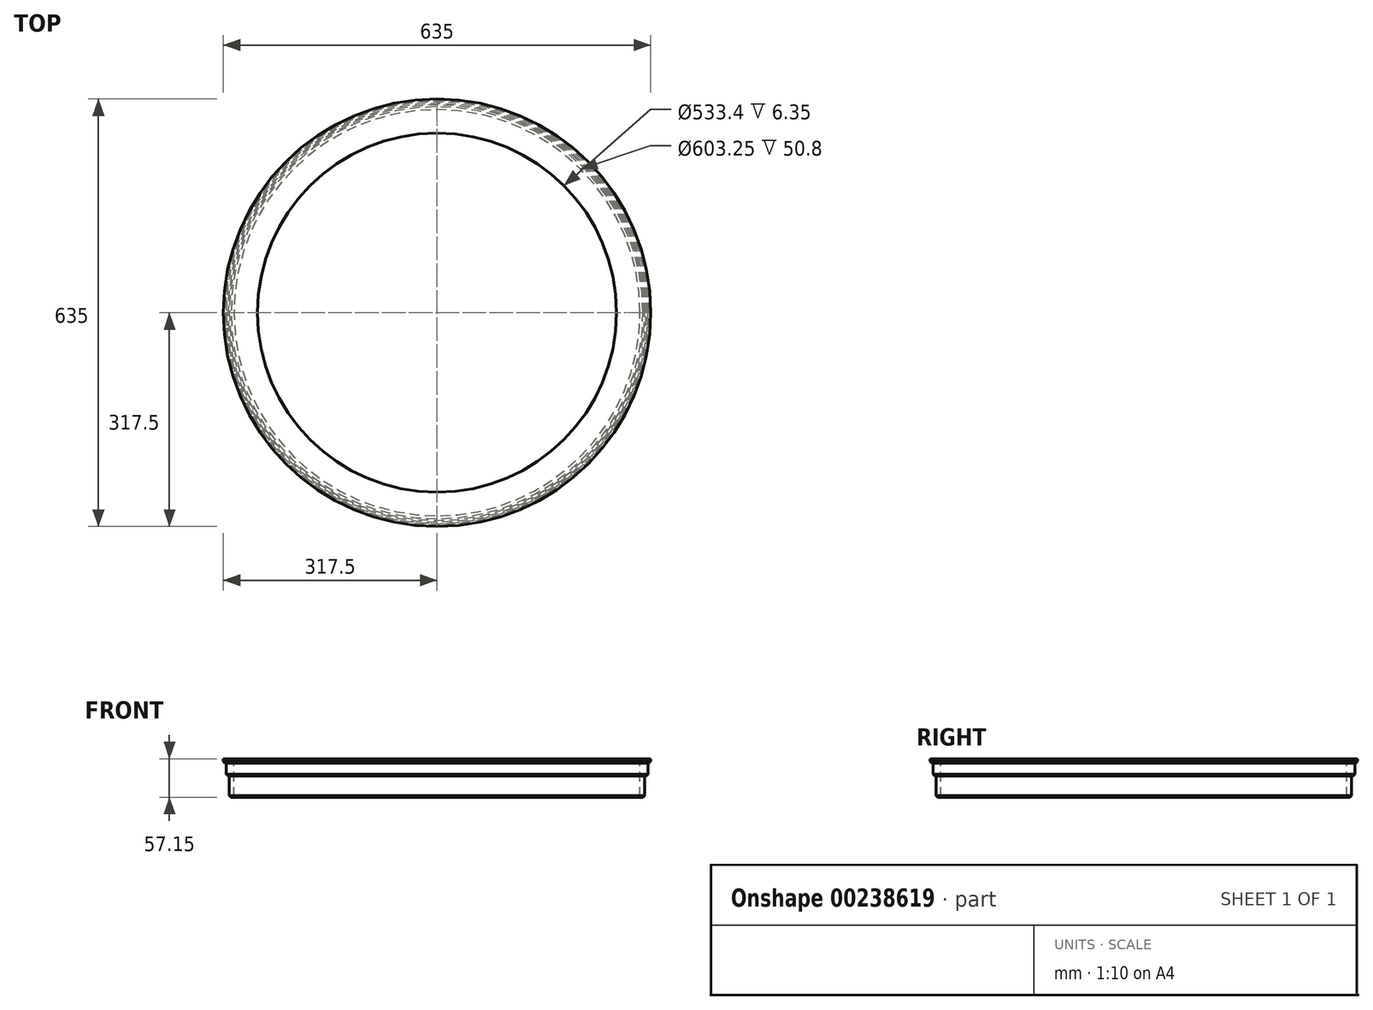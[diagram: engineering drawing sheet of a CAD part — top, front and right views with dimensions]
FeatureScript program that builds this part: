
annotation { "Feature Type Name" : "Feature", "Feature Type Description" : "" }
export const myFeature = defineFeature(function(context is Context, id is Id, definition is map)
    precondition{}
    {
        {
            var Q0;
            Q0=qCreatedBy(makeId("Top.planeOp"),FACE);
            var sketch = newSketch(context, id + "F0", { "sketchPlane" : qUnion([Q0])});
            skCircle(sketch, "E0", {"center": v(0, 0) * mm, "radius": 317.5 * mm});
            skCircle(sketch, "E1", {"center": v(0, 0) * mm, "radius": 266.7 * mm});
            skSolve(sketch);
        }
        {
            var Q0;
            Q0=makeQuery(id+"F0.imprint","IMPRINT",FACE,{"disambiguationData":[TD([[makeQuery(id+"F0.imprint","IMPRINT",EDGE,{"derivedFrom":sQuery(id+"F0.wireOp",EDGE,"E0")}),1.0]])]});
            extrude(context, id + "F1", {"entities" : qUnion([Q0]), "depth" : 6.35 * mm});
        }
        {
            var Q0;
            Q0=makeQuery(id+"F1.opExtrude","CAP_FACE",FACE,{"disambiguationData":[OSD([sQuery(id+"F0.wireOp",EDGE,"E0"),sQuery(id+"F0.wireOp",EDGE,"E1")])],"isStart":true});
            var sketch = newSketch(context, id + "F2", { "sketchPlane" : qUnion([Q0])});
            skCircle(sketch, "E2", {"center": v(0, 0) * mm, "radius": 301.63 * mm});
            skCircle(sketch, "E3", {"center": v(0, 0) * mm, "radius": 308.61 * mm});
            skCircle(sketch, "E4", {"center": v(0, 0) * mm, "radius": 313.38 * mm});
            skSolve(sketch);
        }
        {
            var Q0;
            Q0=makeQuery(id+"F2.imprint","IMPRINT",FACE,{"disambiguationData":[TD([[makeQuery(id+"F2.imprint","IMPRINT",EDGE,{"derivedFrom":sQuery(id+"F2.wireOp",EDGE,"E2")}),-1.0]])]});
            extrude(context, id + "F3", {"entities" : qUnion([Q0]), "operationType" : NewBodyOperationType.ADD, "depth" : 50.8 * mm});
        }
        {
            var Q0;
            Q0=makeQuery(id+"F2.imprint","IMPRINT",FACE,{"disambiguationData":[TD([[makeQuery(id+"F2.imprint","IMPRINT",EDGE,{"derivedFrom":sQuery(id+"F2.wireOp",EDGE,"E3")}),-1.0]])]});
            extrude(context, id + "F4", {"entities" : qUnion([Q0]), "operationType" : NewBodyOperationType.ADD, "depth" : 19.05 * mm});
        }
        {
            var Q0;
            Q0=makeQuery(id+"F4.opExtrude","CAP_EDGE",EDGE,{"disambiguationData":[OSD([sQuery(id+"F2.wireOp",EDGE,"E4")])],"isStart":false});
            var Q1;
            Q1=makeQuery(id+"F1.opExtrude","CAP_EDGE",EDGE,{"disambiguationData":[OSD([sQuery(id+"F0.wireOp",EDGE,"E0")])],"isStart":true});
            var Q2;
            Q2=makeQuery(id+"F3.opExtrude","CAP_EDGE",EDGE,{"disambiguationData":[OSD([sQuery(id+"F2.wireOp",EDGE,"E3")])],"isStart":false});
            chamfer(context, id + "F5", {"entities" : qUnion([Q0, Q1, Q2]), "width" : 2.54 * mm, "tangentPropagation" : true});
        }
    });
